# Revit family: ADB Electric cooktops cupboard 400
name_source: partatom
category: Equipement spécialisé
units: mm (PartAtom-declared; Revit-internal decimal feet)

## family parameters
Basée sur le plan de construction = Non
Conserver l'orientation des annotations = Non
Cote de connecteur circulaire = Utiliser le diamètre
Couper avec des vides une fois chargée = Non
Numéro OmniClass = 23.40.40.14.17.11
Partagée = Non
Repère de localisation dans la pièce = Non
Titre OmniClass = Cookers, Ovens, Stoves
Toujours verticalement = Oui
Type d'élément = Normal

## types (4) — shared parameters
C = 200 mm  [stored 0.656168 ft]
Commentaires du type = Ambassade range - Cupboards - Electric cooktops
D = 765 mm  [stored 2.50984 ft]
Fabricant = Société Industrielle de Lacanche
URL = https://www.ambassade-de-bourgogne.com
URL Cutsheet = https://www.ambassade-de-bourgogne.com
zero-valued in all types: Elévation par défaut

## per-type parameters (varying)
| type | Description | E | Electric power | Electrical Remarks | Operational Current | Poids base | Table | VTR |
| CME 420 VTR | 2x2.1kW radiant ring electric cupboard | Non | 4200 W | 230V(MONO) commutable 400V(TRI) | 18 A | 52.00 kg | 2 foyers radiants | Oui |
| CME 420 E | 2x2kW hotplate electric cupboard | Oui | 4000 W | 230V(MONO) commutable 400V(TRI), 400V TRI sans neutre en option | 17 A | 42.00 kg | 2 plaques électriques : 420 E | Non |
| CME 423 VTR | 3,5kW+1,2kW radiant ring electric cupboard | Non | 4700 W | 230V(MONO) commutable 400V(TRI) | 20 A | 53.00 kg | 2 foyers radiants | Oui |
| CME 423 E | 2kW+2,6kW hotplate electric cupboard | Oui | 4600 W | 230V(MONO) commutable 400V(TRI), 400V TRI sans neutre en option | 20 A | 43.00 kg | 2 plaques électriques : 423 E | Non |

note: column(s) folded — value = type name in every type: Modèle

note: [stored X ft] marks values corroborated as IEEE doubles in the binary element streams (Revit-internal decimal feet)
